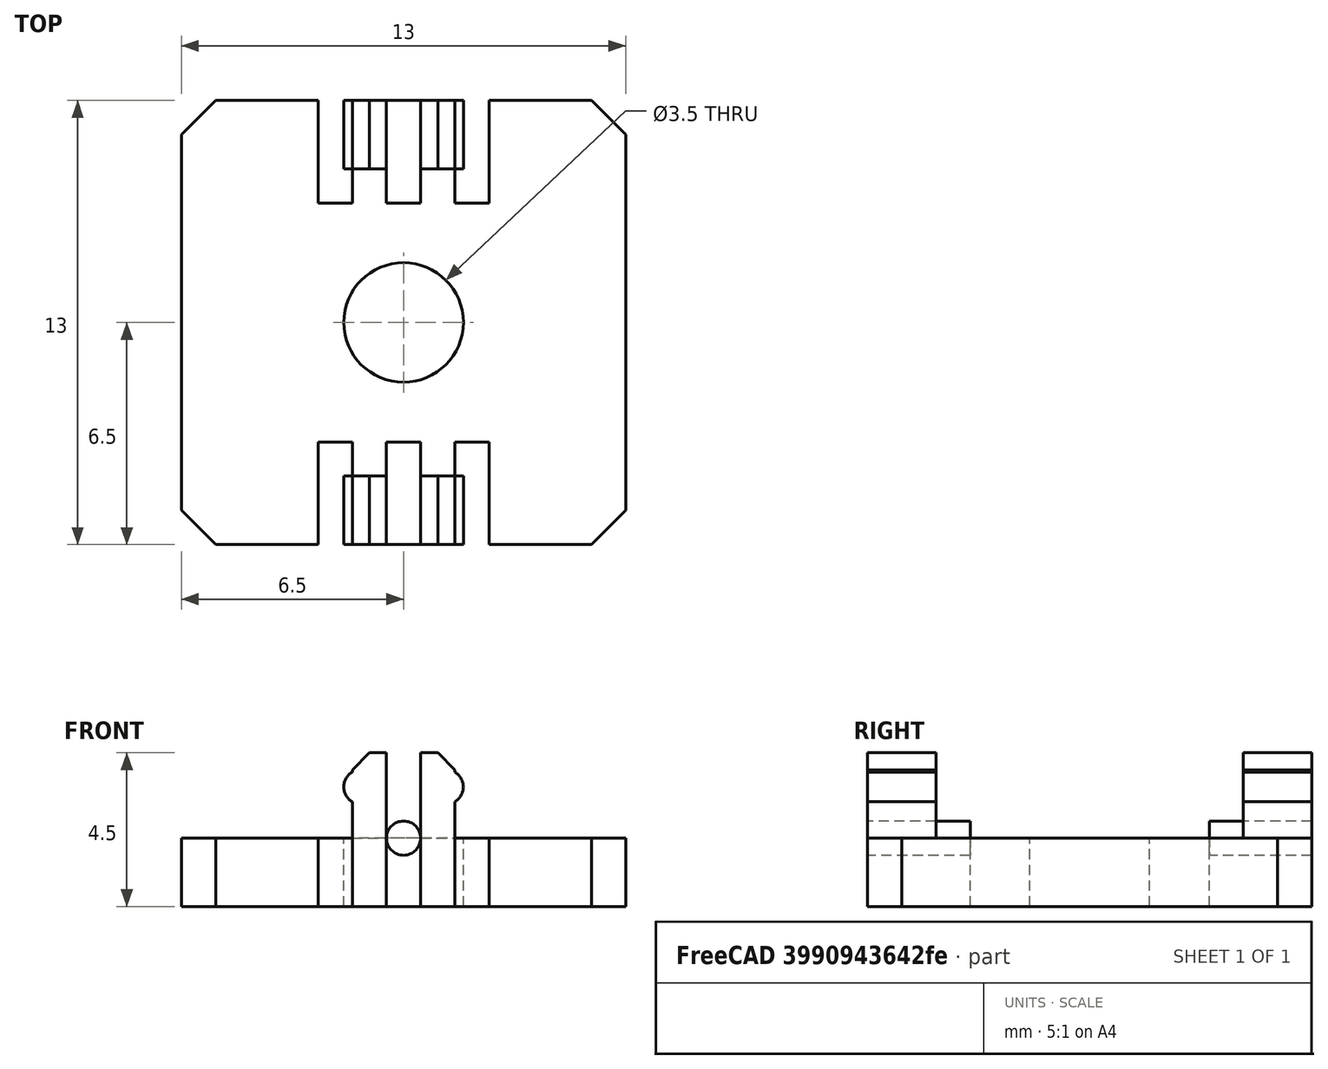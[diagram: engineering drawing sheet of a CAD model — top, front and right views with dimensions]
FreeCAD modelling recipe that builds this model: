
FCSTD DOCUMENT  (FreeCAD 0.18R16146 (Git))
Label: back-plate-spacer
License: All rights reserved
LicenseURL: http://en.wikipedia.org/wiki/All_rights_reserved
objects: Part::Box×9, Part::MultiFuse×7, Part::Cylinder×5, Part::Cut×3, Part::Chamfer×2, Part::Feature×2
note: 28 computed .brp shape members not serialized (recipe doc carries the construction recipe); baked Part::Feature solids carry a one-line shape summary decoded from their .brp

FEATURE [Part::Box] Box  label="Cube"
  AttacherType = Attacher::AttachEngine3D
  Height = 2
  Length = 13
  Placement = pos=(-6.5,-6.5,0) rot=(0,0,1;0rad)
  Width = 13
FEATURE [Part::Box] Box001  label="Cube001"
  AttacherType = Attacher::AttachEngine3D
  Height = 4.5
  Length = 1
  Placement = pos=(-1.5,4.5,0) rot=(0,0,1;0rad)
  Width = 2
FEATURE [Part::Box] Box002  label="Cube002"
  AttacherType = Attacher::AttachEngine3D
  Height = 4.5
  Length = 1
  Placement = pos=(-1.5,-6.5,0) rot=(0,0,1;0rad)
  Width = 2
FEATURE [Part::Chamfer] Chamfer
  Base = -> Box
  Edges = 4 edges r=1: [Edge1,Edge3,Edge5,Edge7]
FEATURE [Part::Cylinder] Cylinder
  Angle = 360
  AttacherType = Attacher::AttachEngine3D
  Height = 10
  Radius = 1.75
FEATURE [Part::Cut] Cut
  Base = -> Chamfer
  Tool = -> Cylinder
FEATURE [Part::Box] Box003  label="Cube003"
  AttacherType = Attacher::AttachEngine3D
  Height = 4.5
  Length = 1
  Placement = pos=(0.5,-6.5,0) rot=(0,0,1;0rad)
  Width = 2
FEATURE [Part::Box] Box004  label="Cube004"
  AttacherType = Attacher::AttachEngine3D
  Height = 4.5
  Length = 1
  Placement = pos=(0.5,4.5,0) rot=(0,0,1;0rad)
  Width = 2
FEATURE [Part::Cylinder] Cylinder001
  Angle = 360
  AttacherType = Attacher::AttachEngine3D
  Height = 2
  Placement = pos=(-1.25,-6.5,3.5) rot=(1,0,0;4.71239rad)
  Radius = 0.5
FEATURE [Part::Cylinder] Cylinder002
  Angle = 360
  AttacherType = Attacher::AttachEngine3D
  Height = 2
  Placement = pos=(1.25,-6.5,3.5) rot=(-1,0,0;1.5708rad)
  Radius = 0.5
FEATURE [Part::MultiFuse] Fusion
  Shapes = -> [Box002,Box003,Box001,Box004]
FEATURE [Part::Chamfer] Chamfer001
  Base = -> Fusion
  Edges = 4 edges r=0.5: [Edge2,Edge18,Edge26,Edge42]
FEATURE [Part::MultiFuse] Fusion001
  Shapes = -> [Cylinder002,Cylinder001]
FEATURE [Part::Feature] Fusion001001  label="Fusion002"
  Placement = pos=(0,11,0) rot=(0,0,1;0rad)
  shape: bbox 3.5 x 2 x 1 mm, 6 faces, 2 solids (baked)
FEATURE [Part::MultiFuse] Fusion001002
  Shapes = -> [Fusion001001,Fusion001,Chamfer001,Cut]
FEATURE [Part::Cylinder] Cylinder003
  Angle = 360
  AttacherType = Attacher::AttachEngine3D
  Height = 3
  Placement = pos=(0,-3.5,2) rot=(1,0,0;1.5708rad)
  Radius = 0.5
FEATURE [Part::Cylinder] Cylinder004
  Angle = 360
  AttacherType = Attacher::AttachEngine3D
  Height = 3
  Placement = pos=(0,6.5,2) rot=(1,0,0;1.5708rad)
  Radius = 0.5
FEATURE [Part::MultiFuse] Fusion001003
  Shapes = -> [Cylinder004,Cylinder003]
FEATURE [Part::Box] Box005  label="Cube005"
  AttacherType = Attacher::AttachEngine3D
  Height = 3
  Length = 1
  Placement = pos=(-2.5,-6.5,0) rot=(0,0,1;0rad)
  Width = 3
FEATURE [Part::Box] Box006  label="Cube006"
  AttacherType = Attacher::AttachEngine3D
  Height = 3
  Length = 1
  Placement = pos=(1.5,-6.5,0) rot=(0,0,1;0rad)
  Width = 3
FEATURE [Part::MultiFuse] Fusion001004
  Shapes = -> [Box006,Box005]
FEATURE [Part::Feature] Fusion001004001  label="Fusion001005"
  Placement = pos=(0,10,0) rot=(0,0,1;0rad)
  shape: bbox 5 x 3 x 3 mm, 12 faces, 2 solids (baked)
FEATURE [Part::MultiFuse] Fusion001004002
  Shapes = -> [Fusion001004001,Fusion001004]
FEATURE [Part::Cut] Cut001
  Base = -> Fusion001002
  Tool = -> Fusion001004002
FEATURE [Part::Box] Box007  label="Cube007"
  AttacherType = Attacher::AttachEngine3D
  Height = 4
  Length = 1
  Placement = pos=(-0.5,-6.5,0) rot=(0,0,1;0rad)
  Width = 3
FEATURE [Part::Box] Box008  label="Cube008"
  AttacherType = Attacher::AttachEngine3D
  Height = 4
  Length = 1
  Placement = pos=(-0.5,3.5,0) rot=(0,0,1;0rad)
  Width = 3
FEATURE [Part::MultiFuse] Fusion001004003
  Shapes = -> [Box008,Box007]
FEATURE [Part::Cut] Cut002
  Base = -> Cut001
  Tool = -> Fusion001004003
